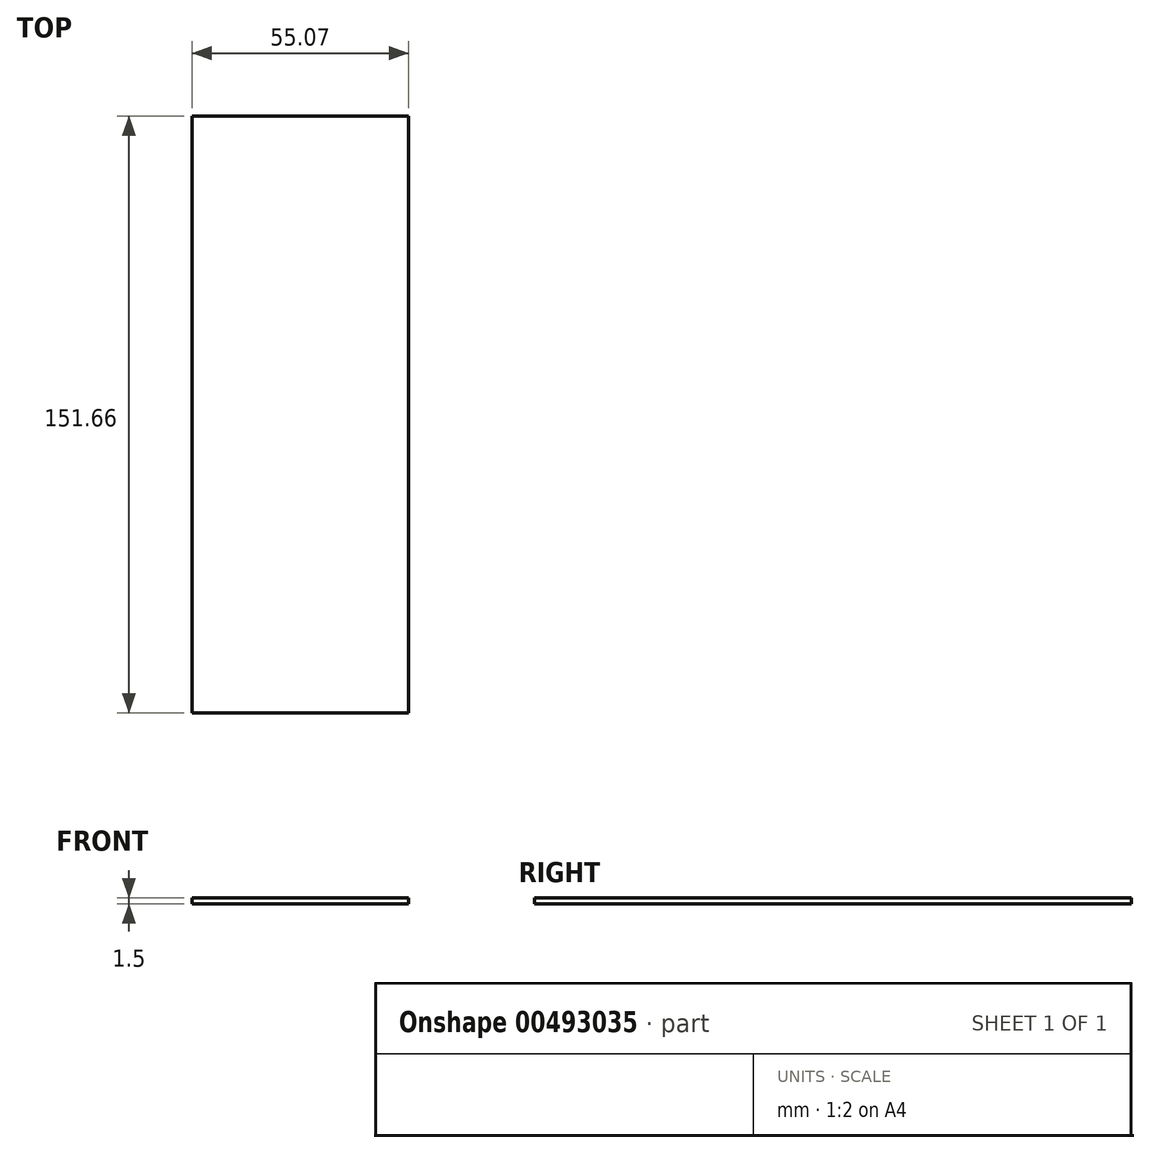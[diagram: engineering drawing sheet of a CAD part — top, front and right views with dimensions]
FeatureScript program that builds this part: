
annotation { "Feature Type Name" : "Feature", "Feature Type Description" : "" }
export const myFeature = defineFeature(function(context is Context, id is Id, definition is map)
    precondition{}
    {
        {
            var Q0;
            Q0=qCreatedBy(makeId("Top.planeOp"),FACE);
            var sketch = newSketch(context, id + "F0", { "sketchPlane" : qUnion([Q0])});
            skLineSegment(sketch, "E0.bottom", {"start": v(-55.07, -76.1) * mm, "end": v(0, -76.1) * mm});
            skLineSegment(sketch, "E0.top", {"start": v(-55.07, 75.56) * mm, "end": v(0, 75.56) * mm});
            skLineSegment(sketch, "E0.left", {"start": v(-55.07, -76.1) * mm, "end": v(-55.07, 75.56) * mm});
            skLineSegment(sketch, "E0.right", {"start": v(0, -76.1) * mm, "end": v(0, 75.56) * mm});
            skSolve(sketch);
        }
        {
            var Q0;
            Q0 = qSketchRegion(id + "F0", true);
            extrude(context, id + "F1", {"entities" : qUnion([Q0]), "depth" : 1.5 * mm});
        }
    });
